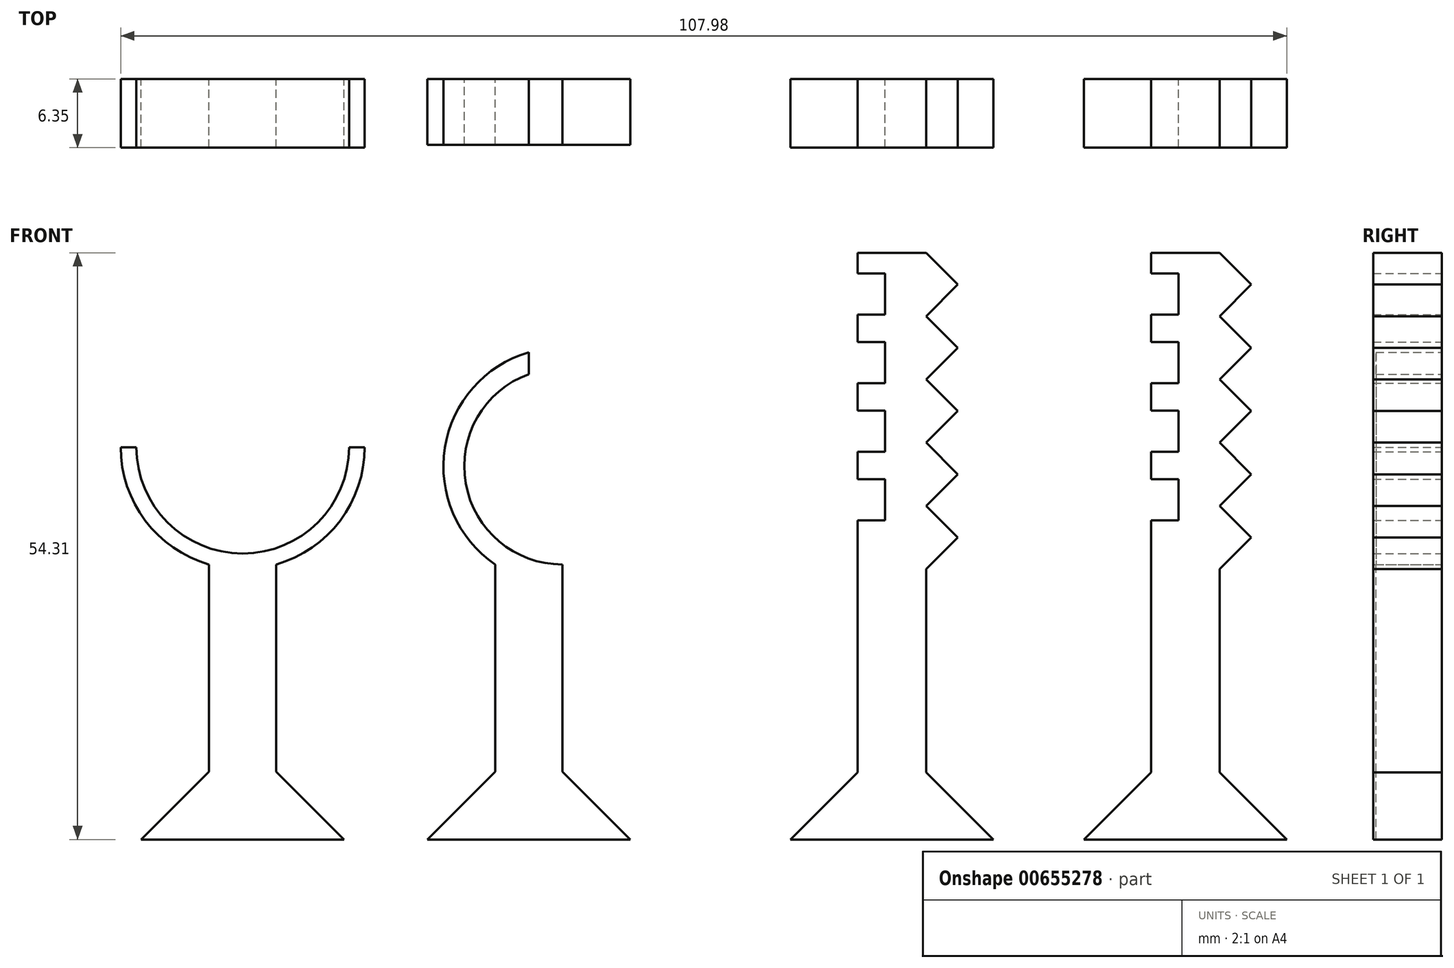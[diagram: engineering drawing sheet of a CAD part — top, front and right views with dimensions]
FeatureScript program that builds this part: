
annotation { "Feature Type Name" : "Feature", "Feature Type Description" : "" }
export const myFeature = defineFeature(function(context is Context, id is Id, definition is map)
    precondition{}
    {
        {
            var Q0;
            Q0=qCreatedBy(makeId("Front.planeOp"),FACE);
            var sketch = newSketch(context, id + "F0", { "sketchPlane" : qUnion([Q0])});
            skLineSegment(sketch, "E0", {"start": v(0, 0) * mm, "end": v(-9.4, 0) * mm});
            skLineSegment(sketch, "E1", {"start": v(-9.4, 0) * mm, "end": v(-3.11, 6.29) * mm});
            skLineSegment(sketch, "E2", {"start": v(-3.11, 6.29) * mm, "end": v(-3.11, 25.46) * mm});
            skLineSegment(sketch, "E3", {"start": v(-3.11, 25.46) * mm, "end": v(0, 25.46) * mm});
            skLineSegment(sketch, "E4.MirrorCS", {"start": v(3.11, 25.46) * mm, "end": v(0, 25.46) * mm});
            skLineSegment(sketch, "E5.MirrorCS", {"start": v(3.11, 6.29) * mm, "end": v(3.11, 25.46) * mm});
            skLineSegment(sketch, "E6.MirrorCS", {"start": v(9.4, 0) * mm, "end": v(3.11, 6.29) * mm});
            skLineSegment(sketch, "E7.MirrorCS", {"start": v(0, 0) * mm, "end": v(9.4, 0) * mm});
            skArc(sketch, "E8", {"start": v(3.11, 25.46) * mm, "mid": v(-5.84, 32.97) * mm, "end": v(0, 43.08) * mm});
            skArc(sketch, "E9", {"start": v(-3.11, 25.46) * mm, "mid": v(-7.77, 36.27) * mm, "end": v(0, 45.11) * mm});
            skLineSegment(sketch, "E10", {"start": v(0, 43.08) * mm, "end": v(0, 45.11) * mm});
            skSolve(sketch);
        }
        {
            var Q0;
            Q0=makeQuery(id+"F0.imprint","IMPRINT",FACE,{"disambiguationData":[TD([[makeQuery(id+"F0.imprint","IMPRINT",EDGE,{"derivedFrom":sQuery(id+"F0.wireOp",EDGE,"E0")}),-1.0]])]});
            var Q1;
            Q1=makeQuery(id+"F0.imprint","IMPRINT",FACE,{"disambiguationData":[TD([[makeQuery(id+"F0.imprint","IMPRINT",EDGE,{"derivedFrom":sQuery(id+"F0.wireOp",EDGE,"E3")}),1.0]])]});
            extrude(context, id + "F1", {"entities" : qUnion([Q0, Q1]), "depth" : 6.1 * mm, "offsetDistance" : 25.4 * mm});
        }
        {
            var Q0;
            Q0=qCreatedBy(makeId("Front.planeOp"),FACE);
            var sketch = newSketch(context, id + "F2", { "sketchPlane" : qUnion([Q0])});
            skLineSegment(sketch, "E11", {"start": v(-35.89, 0) * mm, "end": v(-17.09, 0) * mm});
            skLineSegment(sketch, "E12", {"start": v(-17.09, 0) * mm, "end": v(-23.38, 6.29) * mm});
            skLineSegment(sketch, "E13", {"start": v(-23.38, 6.29) * mm, "end": v(-23.38, 25.46) * mm});
            skLineSegment(sketch, "E14", {"start": v(-23.38, 25.46) * mm, "end": v(-29.6, 25.46) * mm});
            skLineSegment(sketch, "E15", {"start": v(-29.6, 25.46) * mm, "end": v(-29.6, 6.29) * mm});
            skLineSegment(sketch, "E16", {"start": v(-29.6, 6.29) * mm, "end": v(-35.89, 0) * mm});
            skArc(sketch, "E17", {"start": v(-29.6, 25.46) * mm, "mid": v(-35.5, 29.52) * mm, "end": v(-37.78, 36.32) * mm});
            skPoint(sketch, "E17.centerSnap0", {"position": v(-26.49, 25.46) * mm});
            skArc(sketch, "E18", {"start": v(-23.38, 25.46) * mm, "mid": v(-17.47, 29.52) * mm, "end": v(-15.2, 36.32) * mm});
            skArc(sketch, "E19", {"start": v(-16.64, 36.32) * mm, "mid": v(-26.49, 26.48) * mm, "end": v(-36.33, 36.32) * mm});
            skLineSegment(sketch, "E20", {"start": v(-15.2, 36.32) * mm, "end": v(-16.64, 36.32) * mm});
            skLineSegment(sketch, "E21", {"start": v(-36.33, 36.32) * mm, "end": v(-37.78, 36.32) * mm});
            skSolve(sketch);
        }
        {
            var Q0;
            Q0 = qSketchRegion(id + "F2", true);
            extrude(context, id + "F3", {"entities" : qUnion([Q0]), "depth" : 6.35 * mm, "offsetDistance" : 25.4 * mm});
        }
        {
            var Q0;
            Q0=qCreatedBy(makeId("Front.planeOp"),FACE);
            var sketch = newSketch(context, id + "F4", { "sketchPlane" : qUnion([Q0])});
            skLineSegment(sketch, "E22", {"start": v(24.22, 0) * mm, "end": v(43.02, 0) * mm});
            skLineSegment(sketch, "E23", {"start": v(43.02, 0) * mm, "end": v(36.8, 6.22) * mm});
            skLineSegment(sketch, "E24", {"start": v(36.8, 6.22) * mm, "end": v(36.8, 54.3) * mm});
            skLineSegment(sketch, "E25", {"start": v(36.8, 54.3) * mm, "end": v(30.44, 54.3) * mm});
            skLineSegment(sketch, "E26", {"start": v(30.44, 54.3) * mm, "end": v(30.44, 6.22) * mm});
            skLineSegment(sketch, "E27", {"start": v(30.44, 6.22) * mm, "end": v(24.22, 0) * mm});
            skLineSegment(sketch, "E28", {"start": v(36.8, 54.3) * mm, "end": v(39.72, 51.38) * mm});
            skLineSegment(sketch, "E29", {"start": v(39.72, 51.38) * mm, "end": v(36.8, 48.45) * mm});
            skLineSegment(sketch, "E30", {"start": v(36.8, 48.45) * mm, "end": v(39.72, 45.52) * mm});
            skLineSegment(sketch, "E31", {"start": v(39.72, 45.52) * mm, "end": v(36.8, 42.6) * mm});
            skLineSegment(sketch, "E32", {"start": v(36.8, 42.6) * mm, "end": v(39.72, 39.67) * mm});
            skLineSegment(sketch, "E33", {"start": v(39.72, 39.67) * mm, "end": v(36.8, 36.74) * mm});
            skLineSegment(sketch, "E34", {"start": v(36.8, 36.74) * mm, "end": v(39.72, 33.81) * mm});
            skLineSegment(sketch, "E35", {"start": v(39.72, 33.81) * mm, "end": v(36.8, 30.89) * mm});
            skLineSegment(sketch, "E36", {"start": v(36.8, 30.89) * mm, "end": v(39.72, 27.96) * mm});
            skLineSegment(sketch, "E37", {"start": v(39.72, 27.96) * mm, "end": v(36.8, 25.03) * mm});
            skSolve(sketch);
        }
        {
            var Q0;
            Q0 = qSketchRegion(id + "F4", true);
            extrude(context, id + "F5", {"entities" : qUnion([Q0]), "depth" : 6.35 * mm, "offsetDistance" : 25.4 * mm});
        }
        {
            var Q0;
            Q0=makeQuery(id+"F5.opExtrude","CAP_FACE",FACE,{"disambiguationData":[OSD([sQuery(id+"F4.wireOp",EDGE,"E22"),sQuery(id+"F4.wireOp",EDGE,"E23"),sQuery(id+"F4.wireOp",EDGE,"E24"),sQuery(id+"F4.wireOp",EDGE,"E25"),sQuery(id+"F4.wireOp",EDGE,"E26"),sQuery(id+"F4.wireOp",EDGE,"E27"),sQuery(id+"F4.wireOp",EDGE,"E28"),sQuery(id+"F4.wireOp",EDGE,"E29"),sQuery(id+"F4.wireOp",EDGE,"E30"),sQuery(id+"F4.wireOp",EDGE,"E31"),sQuery(id+"F4.wireOp",EDGE,"E32"),sQuery(id+"F4.wireOp",EDGE,"E33"),sQuery(id+"F4.wireOp",EDGE,"E34"),sQuery(id+"F4.wireOp",EDGE,"E35"),sQuery(id+"F4.wireOp",EDGE,"E36"),sQuery(id+"F4.wireOp",EDGE,"E37")])],"isStart":true});
            var sketch = newSketch(context, id + "F6", { "sketchPlane" : qUnion([Q0])});
            skLineSegment(sketch, "E38.bottom", {"start": v(-32.98, 48.6) * mm, "end": v(-27.9, 48.6) * mm});
            skLineSegment(sketch, "E38.top", {"start": v(-32.98, 52.4) * mm, "end": v(-27.9, 52.4) * mm});
            skLineSegment(sketch, "E38.left", {"start": v(-32.98, 48.6) * mm, "end": v(-32.98, 52.4) * mm});
            skLineSegment(sketch, "E38.right", {"start": v(-27.9, 48.6) * mm, "end": v(-27.9, 52.4) * mm});
            skPoint(sketch, "E38.middle", {"position": v(-30.44, 50.5) * mm});
            skLineSegment(sketch, "E39.bottom", {"start": v(-32.98, 42.24) * mm, "end": v(-27.9, 42.24) * mm});
            skLineSegment(sketch, "E39.top", {"start": v(-32.98, 46.05) * mm, "end": v(-27.9, 46.05) * mm});
            skLineSegment(sketch, "E39.left", {"start": v(-32.98, 42.24) * mm, "end": v(-32.98, 46.05) * mm});
            skLineSegment(sketch, "E39.right", {"start": v(-27.9, 42.24) * mm, "end": v(-27.9, 46.05) * mm});
            skPoint(sketch, "E39.middle", {"position": v(-30.44, 44.15) * mm});
            skLineSegment(sketch, "E40.bottom", {"start": v(-32.98, 35.9) * mm, "end": v(-27.9, 35.9) * mm});
            skLineSegment(sketch, "E40.top", {"start": v(-32.98, 39.7) * mm, "end": v(-27.9, 39.7) * mm});
            skLineSegment(sketch, "E40.left", {"start": v(-32.98, 35.9) * mm, "end": v(-32.98, 39.7) * mm});
            skLineSegment(sketch, "E40.right", {"start": v(-27.9, 35.9) * mm, "end": v(-27.9, 39.7) * mm});
            skPoint(sketch, "E40.middle", {"position": v(-30.44, 37.8) * mm});
            skLineSegment(sketch, "E41.bottom", {"start": v(-32.98, 29.54) * mm, "end": v(-27.9, 29.54) * mm});
            skLineSegment(sketch, "E41.top", {"start": v(-32.98, 33.35) * mm, "end": v(-27.9, 33.35) * mm});
            skLineSegment(sketch, "E41.left", {"start": v(-32.98, 29.54) * mm, "end": v(-32.98, 33.35) * mm});
            skLineSegment(sketch, "E41.right", {"start": v(-27.9, 29.54) * mm, "end": v(-27.9, 33.35) * mm});
            skPoint(sketch, "E41.middle", {"position": v(-30.44, 31.45) * mm});
            skSolve(sketch);
        }
        {
            var Q0;
            Q0 = qSketchRegion(id + "F6", true);
            extrude(context, id + "F7", {"entities" : qUnion([Q0]), "operationType" : NewBodyOperationType.REMOVE, "oppositeDirection" : true, "depth" : 25.4 * mm, "offsetDistance" : 25.4 * mm});
        }
        {
            var Q0;
            Q0=makeQuery(id+"F5.opExtrude","SWEPT_BODY",BODY,{"disambiguationData":[OSD([sQuery(id+"F4.wireOp",EDGE,"E22"),sQuery(id+"F4.wireOp",EDGE,"E23"),sQuery(id+"F4.wireOp",EDGE,"E24"),sQuery(id+"F4.wireOp",EDGE,"E25"),sQuery(id+"F4.wireOp",EDGE,"E26"),sQuery(id+"F4.wireOp",EDGE,"E27"),sQuery(id+"F4.wireOp",EDGE,"E28"),sQuery(id+"F4.wireOp",EDGE,"E29"),sQuery(id+"F4.wireOp",EDGE,"E30"),sQuery(id+"F4.wireOp",EDGE,"E31"),sQuery(id+"F4.wireOp",EDGE,"E32"),sQuery(id+"F4.wireOp",EDGE,"E33"),sQuery(id+"F4.wireOp",EDGE,"E34"),sQuery(id+"F4.wireOp",EDGE,"E35"),sQuery(id+"F4.wireOp",EDGE,"E36"),sQuery(id+"F4.wireOp",EDGE,"E37")])]});
            transform(context, id + "F8", {"entities" : qUnion([Q0]), "transformType" : TransformType.TRANSLATION_3D, "dx" : 27.18 * mm, "dy" : 0 * mm, "dz" : 0 * mm, "makeCopy" : true});
        }
    });
